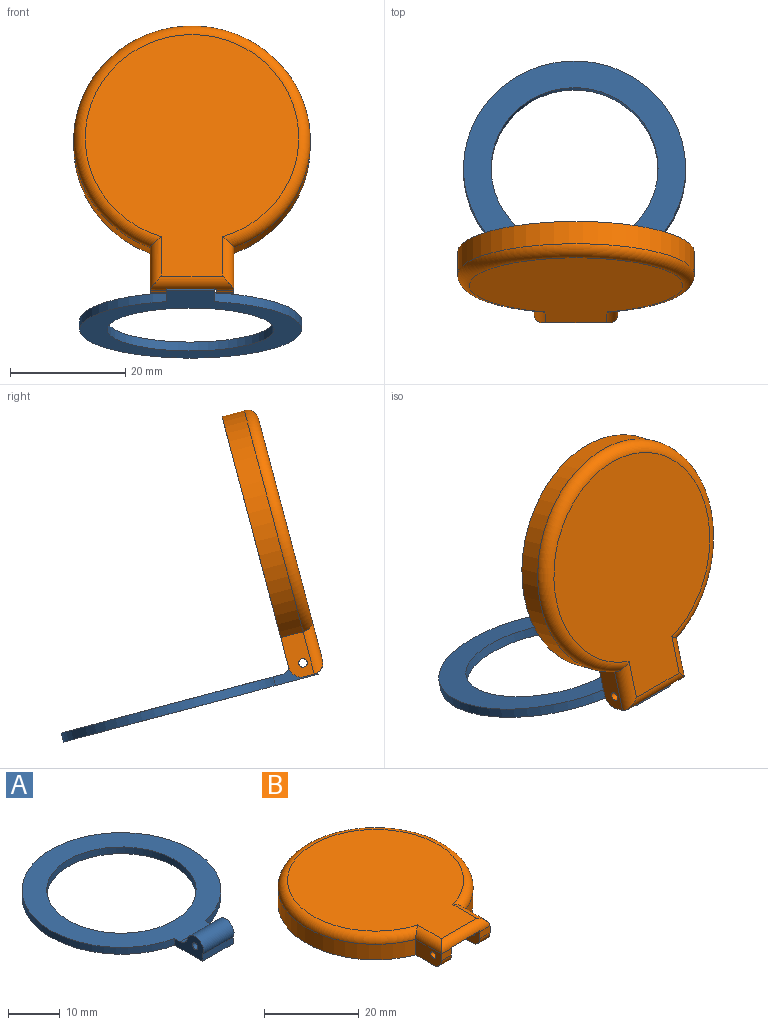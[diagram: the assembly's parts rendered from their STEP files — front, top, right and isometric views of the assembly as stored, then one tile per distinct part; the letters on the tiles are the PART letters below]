
ASSEMBLY  parts=2 mates=1
PART A: 10 faces, bbox 38.6x46x4.9 mm
  f0: plane 7.87x4.85mm, normal (-1,0,0), area 23.5mm2, adj f1,f3,f5,f6,f7,f8,f9
  f1: plane 45.77x38.6mm, normal (0,0,-1), area 571.2mm2, adj f0,f2,f3,f4,f8
  f2: plane 7.87x4.85mm, normal (1,0,0), area 23.5mm2, adj f1,f3,f5,f6,f7,f8,f9
  f3: cylinder r=19.3mm len=38.6mm, axis (0,0,-1), area 180.5mm2, adj f0,f1,f2,f5
  f4: cylinder r=14.5mm len=29mm, axis (0,0,-1), area 145.8mm2, adj f1,f5
  f5: plane 39.62x38.6mm, normal (0,0,1), area 519.6mm2, adj f0,f2,f3,f4,f9
  f6: cylinder r=2.25mm len=8.4mm, axis (1,0,0), area 63.6mm2, adj f0,f2,f8,f9
  f7: cylinder r=0.75mm len=8.4mm, axis (1,0,0), area 39.6mm2, adj f0,f2
  f8: plane 8.4x1.6mm, normal (0,-1,0), area 13.4mm2, adj f0,f1,f2,f6
  f9: cylinder r=2mm len=8.4mm, axis (1,0,0), area 22.4mm2, adj f0,f2,f5,f6
PART B: 25 faces, bbox 44.5x49.1x6 mm
  f0: plane 7.96x4.95mm, normal (1,0,0), area 28.9mm2, adj f5,f6,f7,f10,f12,f13,f14,f17
  f1: plane 38.73x38.7mm, normal (0,0,-1), area 1176.4mm2, adj f5,f22
  f2: plane 3x1.75mm, normal (0,-1,0), area 5.3mm2, adj f3,f11,f15,f19
  f3: plane 7.96x4.95mm, normal (-1,0,0), area 28.9mm2, adj f2,f5,f6,f7,f12,f13,f15,f16
  f4: cylinder r=20.55mm len=41.1mm, axis (0,0,-1), area 457.2mm2, adj f6,f9,f11,f20
  f5: cylinder r=19.35mm len=38.7mm, axis (0,0,-1), area 452mm2, adj f0,f1,f3,f6,f22
  f6: plane 45.14x41.1mm, normal (0,0,-1), area 169.4mm2, adj f0,f3,f4,f5,f9,f11,f14,f15
  f7: plane 8.5x2.46mm, normal (0,0,-1), area 18.1mm2, adj f0,f3,f12,f23
  f8: plane 43.39x37.1mm, normal (0,0,1), area 1149.7mm2, adj f18,f19,f20,f21
  f9: plane 7.61x4mm, normal (-1,0,0), area 27.6mm2, adj f4,f6,f10,f14,f17,f21
  f10: plane 3x1.75mm, normal (0,-1,0), area 5.3mm2, adj f0,f9,f14,f19
  f11: plane 7.61x4mm, normal (1,0,0), area 27.6mm2, adj f2,f4,f6,f15,f16,f18
  f12: cylinder r=2.35mm len=8.5mm, axis (-1,0,0), area 34.7mm2, adj f0,f3,f7,f13
  f13: plane 8.5x0.67mm, normal (0,0,-1), area 5.7mm2, adj f0,f3,f12,f19
  f14: cylinder r=2.25mm len=3mm, axis (1,0,0), area 10.6mm2, adj f0,f6,f9,f10
  f15: cylinder r=2.25mm len=3mm, axis (1,0,0), area 10.6mm2, adj f2,f3,f6,f11
  f16: cylinder r=0.75mm len=3mm, axis (1,0,0), area 14.1mm2, adj f3,f11
  f17: cylinder r=0.75mm len=3mm, axis (1,0,0), area 14.1mm2, adj f0,f9
  f18: cylinder r=2mm len=9.05mm, axis (0,1,0), area 23.2mm2, adj f8,f11,f19,f20
  f19: cylinder r=2mm len=14.5mm, axis (1,0,0), area 39.1mm2, adj f0,f2,f3,f8,f10,f13,f18,f21
  f20: torus R=18.55mm, axis (0,0,1), area 349.5mm2, adj f4,f8,f18,f21
  f21: cylinder r=2mm len=9.05mm, axis (0,-1,0), area 23.2mm2, adj f8,f9,f19,f20
  f22: cylinder r=18.4mm len=8.5mm, axis (0,0,1), area 18.9mm2, adj f1,f5,f24
  f23: cylinder r=18.4mm len=8.5mm, axis (0,0,1), area 18.9mm2, adj f0,f3,f7,f24
  f24: plane 8.5x1.73mm, normal (0,0,-1), area 10.4mm2, adj f0,f3,f22,f23
PLACE A rot(axis=(-1,0,0),14.9deg) t=(-10.82,-69.45,16.17)mm
PLACE B rot(axis=(1,0,0),75.1deg) t=(-10.57,-83.62,47.93)mm
MATE revolute A.f7 <-> B.f16  axis (1,0,0) through (-6.62,-92.42,24.96)mm
